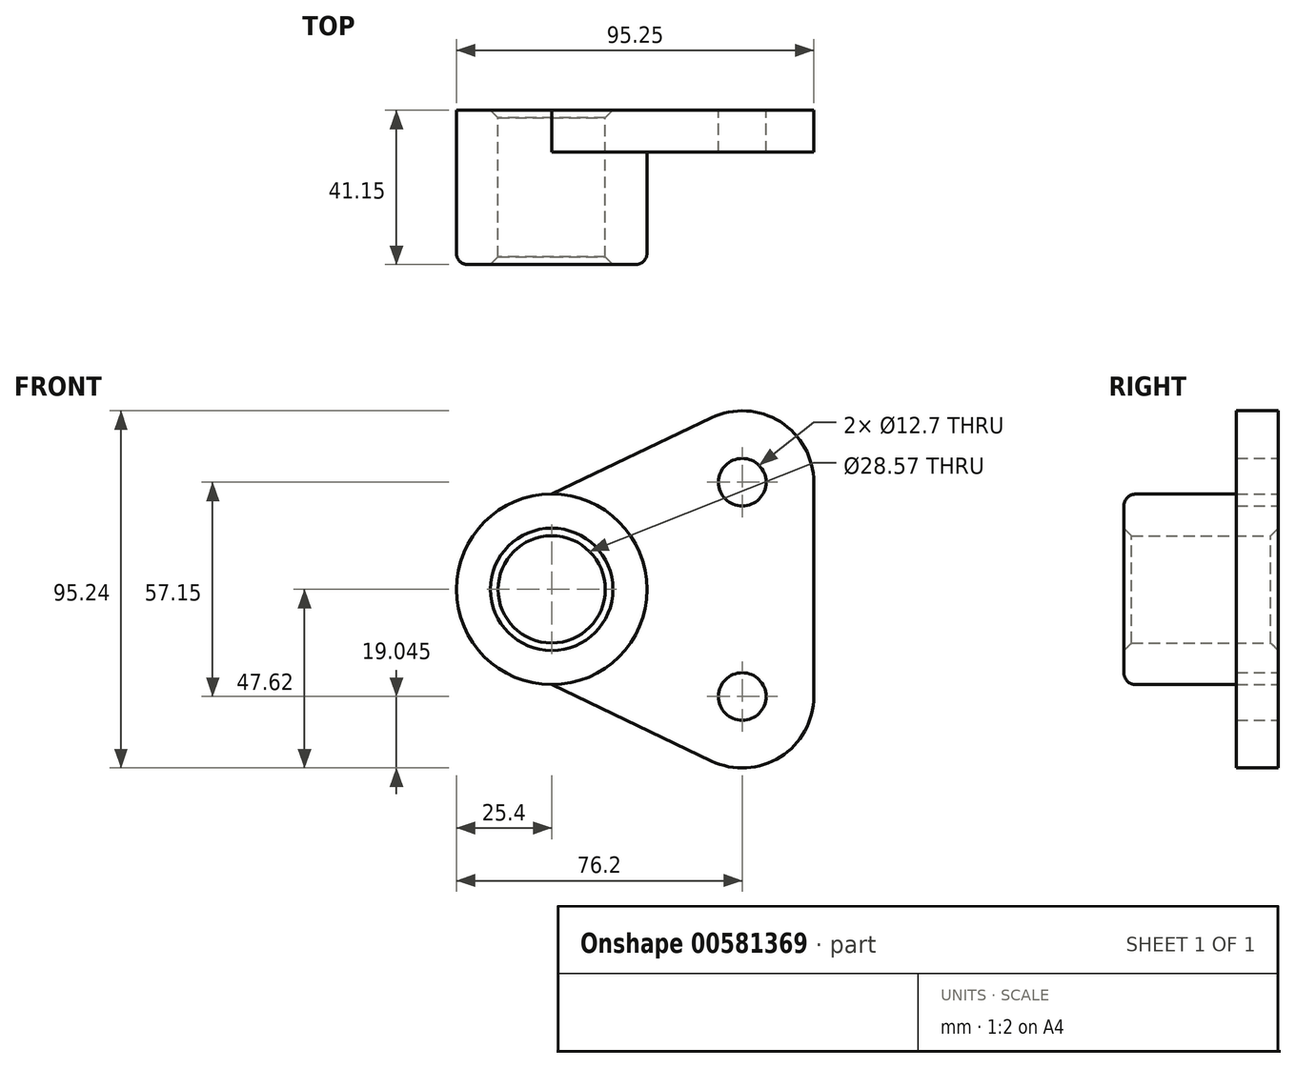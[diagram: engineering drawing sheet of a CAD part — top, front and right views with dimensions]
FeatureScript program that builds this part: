
annotation { "Feature Type Name" : "Feature", "Feature Type Description" : "" }
export const myFeature = defineFeature(function(context is Context, id is Id, definition is map)
    precondition{}
    {
        {
            var Q0;
            Q0=qCreatedBy(makeId("Front.planeOp"),FACE);
            var sketch = newSketch(context, id + "F0", { "sketchPlane" : qUnion([Q0])});
            skCircle(sketch, "E0", {"center": v(-50.8, 0) * mm, "radius": 25.4 * mm});
            skCircle(sketch, "E1", {"center": v(0, -28.58) * mm, "radius": 6.35 * mm});
            skCircle(sketch, "E2", {"center": v(0, 28.58) * mm, "radius": 6.35 * mm});
            skCircle(sketch, "E3", {"center": v(-50.8, 0) * mm, "radius": 14.29 * mm});
            skArc(sketch, "E4", {"start": v(19.05, 28.57) * mm, "mid": v(10.16, 44.7) * mm, "end": v(-8.22, 45.76) * mm});
            skArc(sketch, "E5", {"start": v(-8.22, -45.76) * mm, "mid": v(10.16, -44.7) * mm, "end": v(19.05, -28.58) * mm});
            skLineSegment(sketch, "E6", {"start": v(-50.8, 25.4) * mm, "end": v(-8.22, 45.76) * mm});
            skLineSegment(sketch, "E7", {"start": v(-50.8, -25.4) * mm, "end": v(-8.22, -45.76) * mm});
            skLineSegment(sketch, "E8", {"start": v(19.05, 28.57) * mm, "end": v(19.05, -28.58) * mm});
            skSolve(sketch);
        }
        {
            var Q0;
            Q0=makeQuery(id+"F0.imprint","IMPRINT",FACE,{"disambiguationData":[TD([[makeQuery(id+"F0.imprint","IMPRINT",EDGE,{"derivedFrom":sQuery(id+"F0.wireOp",EDGE,"E3")}),-1.0]])]});
            extrude(context, id + "F1", {"entities" : qUnion([Q0]), "depth" : 41.15 * mm, "offsetDistance" : 25.4 * mm});
        }
        {
            var Q0;
            Q0 = qSketchRegion(id + "F0", true);
            extrude(context, id + "F2", {"entities" : qUnion([Q0]), "operationType" : NewBodyOperationType.ADD, "depth" : 11.18 * mm, "offsetDistance" : 25.4 * mm});
        }
        {
            var Q0;
            Q0=makeQuery(id+"F1.opExtrude","CAP_EDGE",EDGE,{"disambiguationData":[OSD([sQuery(id+"F0.wireOp",EDGE,"E3")])],"isStart":false});
            var Q1;
            Q1=makeQuery(id+"F1.opExtrude","CAP_EDGE",EDGE,{"disambiguationData":[OSD([sQuery(id+"F0.wireOp",EDGE,"E3")])],"isStart":true});
            chamfer(context, id + "F3", {"entities" : qUnion([Q0, Q1]), "chamferType" : ChamferType.OFFSET_ANGLE, "width" : 2.03 * mm, "oppositeDirection" : false, "angle" : 45 * degree, "tangentPropagation" : true});
        }
        {
            var Q0;
            Q0=makeQuery(id+"F1.opExtrude","CAP_EDGE",EDGE,{"disambiguationData":[OSD([sQuery(id+"F0.wireOp",EDGE,"E0")])],"isStart":false});
            fillet(context, id + "F4", {"entities" : qUnion([Q0]), "radius" : 3.05 * mm, "tangentPropagation" : true, "allowEdgeOverflow" : false});
        }
    });
